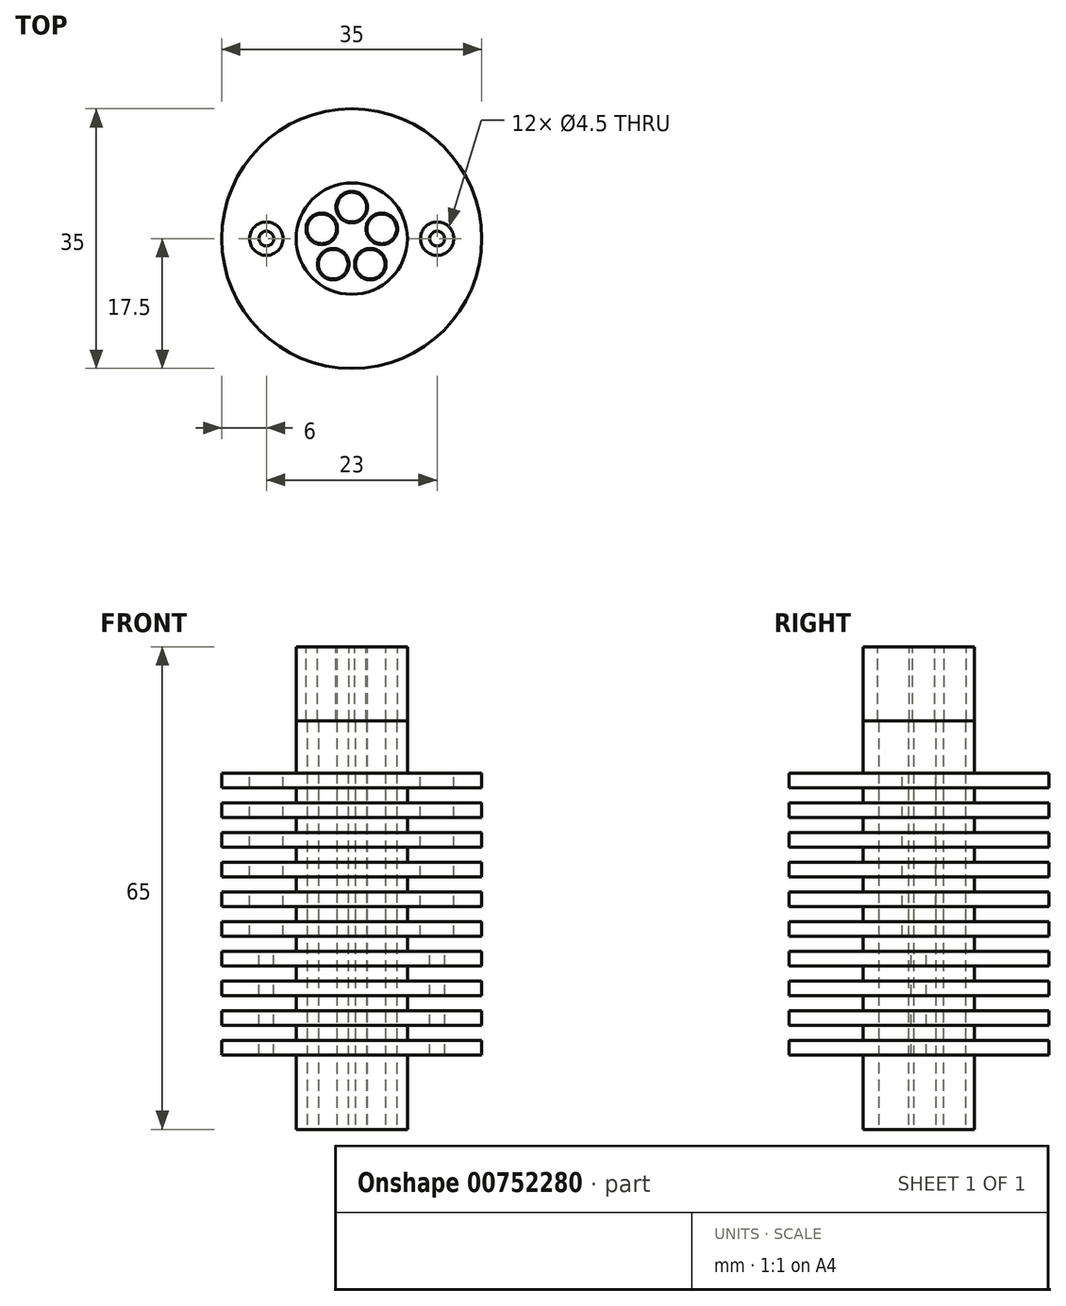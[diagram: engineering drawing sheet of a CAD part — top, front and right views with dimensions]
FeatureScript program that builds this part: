
annotation { "Feature Type Name" : "Feature", "Feature Type Description" : "" }
export const myFeature = defineFeature(function(context is Context, id is Id, definition is map)
    precondition{}
    {
        {
            var Q0;
            Q0=qCreatedBy(makeId("Top.planeOp"),FACE);
            var sketch = newSketch(context, id + "F0", { "sketchPlane" : qUnion([Q0])});
            skCircle(sketch, "E0", {"center": v(0, 0) * mm, "radius": 7.5 * mm});
            skLineSegment(sketch, "E1", {"start": v(0, 0) * mm, "end": v(0, 4.25) * mm});
            skCircle(sketch, "E2", {"center": v(0, 4.25) * mm, "radius": 2 * mm});
            skCircle(sketch, "E3.1.0", {"center": v(-4.04, 1.31) * mm, "radius": 2 * mm});
            skCircle(sketch, "E3.2.0", {"center": v(-2.5, -3.44) * mm, "radius": 2 * mm});
            skCircle(sketch, "E3.3.0", {"center": v(2.5, -3.44) * mm, "radius": 2 * mm});
            skCircle(sketch, "E3.4.0", {"center": v(4.04, 1.31) * mm, "radius": 2 * mm});
            skSolve(sketch);
        }
        {
            var Q0;
            Q0=makeQuery(id+"F0.imprint","IMPRINT",FACE,{"disambiguationData":[TD([[makeQuery(id+"F0.imprint","IMPRINT",EDGE,{"derivedFrom":sQuery(id+"F0.wireOp",EDGE,"E0")}),1.0]])]});
            extrude(context, id + "F1", {"entities" : qUnion([Q0]), "depth" : 50 * mm, "offsetDistance" : 25 * mm});
        }
        {
            var Q0;
            Q0=qCreatedBy(makeId("Front.planeOp"),FACE);
            var sketch = newSketch(context, id + "F2", { "sketchPlane" : qUnion([Q0])});
            skLineSegment(sketch, "E4.bottom", {"start": v(7.5, 5) * mm, "end": v(17.5, 5) * mm});
            skLineSegment(sketch, "E4.top", {"start": v(7.5, 7) * mm, "end": v(17.5, 7) * mm});
            skLineSegment(sketch, "E4.left", {"start": v(7.5, 5) * mm, "end": v(7.5, 7) * mm});
            skLineSegment(sketch, "E4.right", {"start": v(17.5, 5) * mm, "end": v(17.5, 7) * mm});
            skLineSegment(sketch, "E5.1.0.0", {"start": v(7.5, 11) * mm, "end": v(17.5, 11) * mm});
            skLineSegment(sketch, "E5.1.0.1", {"start": v(17.5, 9) * mm, "end": v(17.5, 11) * mm});
            skLineSegment(sketch, "E5.1.0.2", {"start": v(7.5, 9) * mm, "end": v(17.5, 9) * mm});
            skLineSegment(sketch, "E5.1.0.3", {"start": v(7.5, 9) * mm, "end": v(7.5, 11) * mm});
            skLineSegment(sketch, "E5.2.0.0", {"start": v(7.5, 15) * mm, "end": v(17.5, 15) * mm});
            skLineSegment(sketch, "E5.2.0.1", {"start": v(17.5, 13) * mm, "end": v(17.5, 15) * mm});
            skLineSegment(sketch, "E5.2.0.2", {"start": v(7.5, 13) * mm, "end": v(17.5, 13) * mm});
            skLineSegment(sketch, "E5.2.0.3", {"start": v(7.5, 13) * mm, "end": v(7.5, 15) * mm});
            skLineSegment(sketch, "E5.3.0.0", {"start": v(7.5, 19) * mm, "end": v(17.5, 19) * mm});
            skLineSegment(sketch, "E5.3.0.1", {"start": v(17.5, 17) * mm, "end": v(17.5, 19) * mm});
            skLineSegment(sketch, "E5.3.0.2", {"start": v(7.5, 17) * mm, "end": v(17.5, 17) * mm});
            skLineSegment(sketch, "E5.3.0.3", {"start": v(7.5, 17) * mm, "end": v(7.5, 19) * mm});
            skLineSegment(sketch, "E5.4.0.0", {"start": v(7.5, 23) * mm, "end": v(17.5, 23) * mm});
            skLineSegment(sketch, "E5.4.0.1", {"start": v(17.5, 21) * mm, "end": v(17.5, 23) * mm});
            skLineSegment(sketch, "E5.4.0.2", {"start": v(7.5, 21) * mm, "end": v(17.5, 21) * mm});
            skLineSegment(sketch, "E5.4.0.3", {"start": v(7.5, 21) * mm, "end": v(7.5, 23) * mm});
            skLineSegment(sketch, "E5.5.0.0", {"start": v(7.5, 27) * mm, "end": v(17.5, 27) * mm});
            skLineSegment(sketch, "E5.5.0.1", {"start": v(17.5, 25) * mm, "end": v(17.5, 27) * mm});
            skLineSegment(sketch, "E5.5.0.2", {"start": v(7.5, 25) * mm, "end": v(17.5, 25) * mm});
            skLineSegment(sketch, "E5.5.0.3", {"start": v(7.5, 25) * mm, "end": v(7.5, 27) * mm});
            skLineSegment(sketch, "E5.6.0.0", {"start": v(7.5, 31) * mm, "end": v(17.5, 31) * mm});
            skLineSegment(sketch, "E5.6.0.1", {"start": v(17.5, 29) * mm, "end": v(17.5, 31) * mm});
            skLineSegment(sketch, "E5.6.0.2", {"start": v(7.5, 29) * mm, "end": v(17.5, 29) * mm});
            skLineSegment(sketch, "E5.6.0.3", {"start": v(7.5, 29) * mm, "end": v(7.5, 31) * mm});
            skLineSegment(sketch, "E5.7.0.0", {"start": v(7.5, 35) * mm, "end": v(17.5, 35) * mm});
            skLineSegment(sketch, "E5.7.0.1", {"start": v(17.5, 33) * mm, "end": v(17.5, 35) * mm});
            skLineSegment(sketch, "E5.7.0.2", {"start": v(7.5, 33) * mm, "end": v(17.5, 33) * mm});
            skLineSegment(sketch, "E5.7.0.3", {"start": v(7.5, 33) * mm, "end": v(7.5, 35) * mm});
            skLineSegment(sketch, "E5.8.0.0", {"start": v(7.5, 39) * mm, "end": v(17.5, 39) * mm});
            skLineSegment(sketch, "E5.8.0.1", {"start": v(17.5, 37) * mm, "end": v(17.5, 39) * mm});
            skLineSegment(sketch, "E5.8.0.2", {"start": v(7.5, 37) * mm, "end": v(17.5, 37) * mm});
            skLineSegment(sketch, "E5.8.0.3", {"start": v(7.5, 37) * mm, "end": v(7.5, 39) * mm});
            skLineSegment(sketch, "E5.9.0.0", {"start": v(7.5, 43) * mm, "end": v(17.5, 43) * mm});
            skLineSegment(sketch, "E5.9.0.1", {"start": v(17.5, 41) * mm, "end": v(17.5, 43) * mm});
            skLineSegment(sketch, "E5.9.0.2", {"start": v(7.5, 41) * mm, "end": v(17.5, 41) * mm});
            skLineSegment(sketch, "E5.9.0.3", {"start": v(7.5, 41) * mm, "end": v(7.5, 43) * mm});
            skLineSegment(sketch, "E5.direction1", {"start": v(7.5, 5) * mm, "end": v(7.5, 9) * mm, "construction": true});
            skLineSegment(sketch, "E6", {"start": v(0, 0) * mm, "end": v(0, 60.8) * mm});
            skLineSegment(sketch, "E7.0.10.0", {"start": v(7.5, 47) * mm, "end": v(17.5, 47) * mm});
            skLineSegment(sketch, "E7.3.10.0", {"start": v(17.5, 45) * mm, "end": v(17.5, 47) * mm});
            skLineSegment(sketch, "E7.6.10.0", {"start": v(7.5, 45) * mm, "end": v(17.5, 45) * mm});
            skLineSegment(sketch, "E7.9.10.0", {"start": v(7.5, 45) * mm, "end": v(7.5, 47) * mm});
            skSolve(sketch);
        }
        {
            var Q0;
            Q0=makeQuery(id+"F2.imprint","IMPRINT",FACE,{"disambiguationData":[TD([[makeQuery(id+"F2.imprint","IMPRINT",EDGE,{"derivedFrom":sQuery(id+"F2.wireOp",EDGE,"E4.bottom")}),1.0]])]});
            var Q1;
            Q1=makeQuery(id+"F2.imprint","IMPRINT",FACE,{"disambiguationData":[TD([[makeQuery(id+"F2.imprint","IMPRINT",EDGE,{"derivedFrom":sQuery(id+"F2.wireOp",EDGE,"E5.1.0.0")}),-1.0]])]});
            var Q2;
            Q2=makeQuery(id+"F2.imprint","IMPRINT",FACE,{"disambiguationData":[TD([[makeQuery(id+"F2.imprint","IMPRINT",EDGE,{"derivedFrom":sQuery(id+"F2.wireOp",EDGE,"E5.2.0.0")}),-1.0]])]});
            var Q3;
            Q3=makeQuery(id+"F2.imprint","IMPRINT",FACE,{"disambiguationData":[TD([[makeQuery(id+"F2.imprint","IMPRINT",EDGE,{"derivedFrom":sQuery(id+"F2.wireOp",EDGE,"E5.3.0.0")}),-1.0]])]});
            var Q4;
            Q4=makeQuery(id+"F2.imprint","IMPRINT",FACE,{"disambiguationData":[TD([[makeQuery(id+"F2.imprint","IMPRINT",EDGE,{"derivedFrom":sQuery(id+"F2.wireOp",EDGE,"E5.4.0.0")}),-1.0]])]});
            var Q5;
            Q5=makeQuery(id+"F2.imprint","IMPRINT",FACE,{"disambiguationData":[TD([[makeQuery(id+"F2.imprint","IMPRINT",EDGE,{"derivedFrom":sQuery(id+"F2.wireOp",EDGE,"E5.5.0.0")}),-1.0]])]});
            var Q6;
            Q6=makeQuery(id+"F2.imprint","IMPRINT",FACE,{"disambiguationData":[TD([[makeQuery(id+"F2.imprint","IMPRINT",EDGE,{"derivedFrom":sQuery(id+"F2.wireOp",EDGE,"E5.6.0.0")}),-1.0]])]});
            var Q7;
            Q7=makeQuery(id+"F2.imprint","IMPRINT",FACE,{"disambiguationData":[TD([[makeQuery(id+"F2.imprint","IMPRINT",EDGE,{"derivedFrom":sQuery(id+"F2.wireOp",EDGE,"E5.7.0.0")}),-1.0]])]});
            var Q8;
            Q8=makeQuery(id+"F2.imprint","IMPRINT",FACE,{"disambiguationData":[TD([[makeQuery(id+"F2.imprint","IMPRINT",EDGE,{"derivedFrom":sQuery(id+"F2.wireOp",EDGE,"E5.8.0.0")}),-1.0]])]});
            var Q9;
            Q9=makeQuery(id+"F2.imprint","IMPRINT",FACE,{"disambiguationData":[TD([[makeQuery(id+"F2.imprint","IMPRINT",EDGE,{"derivedFrom":sQuery(id+"F2.wireOp",EDGE,"E5.9.0.0")}),-1.0]])]});
            var Q10;
            Q10=makeQuery(id+"F2.imprint","IMPRINT",FACE,{"disambiguationData":[TD([[makeQuery(id+"F2.imprint","IMPRINT",EDGE,{"derivedFrom":sQuery(id+"F2.wireOp",EDGE,"E5.10.0.0")}),-1.0]])]});
            var Q11;
            Q11=makeQuery(id+"F2.imprint","IMPRINT",FACE,{"disambiguationData":[TD([[makeQuery(id+"F2.imprint","IMPRINT",EDGE,{"derivedFrom":sQuery(id+"F2.wireOp",EDGE,"E5.11.0.0")}),-1.0]])]});
            var Q12;
            Q12=makeQuery(id+"F2.imprint","IMPRINT",FACE,{"disambiguationData":[TD([[makeQuery(id+"F2.imprint","IMPRINT",EDGE,{"derivedFrom":sQuery(id+"F2.wireOp",EDGE,"E5.23.0.0")}),-1.0]])]});
            var Q13;
            Q13=makeQuery(id+"F2.imprint","IMPRINT",FACE,{"disambiguationData":[TD([[makeQuery(id+"F2.imprint","IMPRINT",EDGE,{"derivedFrom":sQuery(id+"F2.wireOp",EDGE,"E5.24.0.0")}),-1.0]])]});
            var Q14;
            Q14=makeQuery(id+"F2.imprint","IMPRINT",FACE,{"disambiguationData":[TD([[makeQuery(id+"F2.imprint","IMPRINT",EDGE,{"derivedFrom":sQuery(id+"F2.wireOp",EDGE,"E5.25.0.0")}),-1.0]])]});
            var Q15;
            Q15=makeQuery(id+"F2.imprint","IMPRINT",FACE,{"disambiguationData":[TD([[makeQuery(id+"F2.imprint","IMPRINT",EDGE,{"derivedFrom":sQuery(id+"F2.wireOp",EDGE,"E5.26.0.0")}),-1.0]])]});
            var Q16;
            Q16=makeQuery(id+"F2.imprint","IMPRINT",FACE,{"disambiguationData":[TD([[makeQuery(id+"F2.imprint","IMPRINT",EDGE,{"derivedFrom":sQuery(id+"F2.wireOp",EDGE,"E5.27.0.0")}),-1.0]])]});
            var Q17;
            Q17=makeQuery(id+"F2.imprint","IMPRINT",FACE,{"disambiguationData":[TD([[makeQuery(id+"F2.imprint","IMPRINT",EDGE,{"derivedFrom":sQuery(id+"F2.wireOp",EDGE,"E5.28.0.0")}),-1.0]])]});
            var Q18;
            Q18=makeQuery(id+"F2.imprint","IMPRINT",FACE,{"disambiguationData":[TD([[makeQuery(id+"F2.imprint","IMPRINT",EDGE,{"derivedFrom":sQuery(id+"F2.wireOp",EDGE,"E5.16.0.0")}),-1.0]])]});
            var Q19;
            Q19=makeQuery(id+"F2.imprint","IMPRINT",FACE,{"disambiguationData":[TD([[makeQuery(id+"F2.imprint","IMPRINT",EDGE,{"derivedFrom":sQuery(id+"F2.wireOp",EDGE,"E5.17.0.0")}),-1.0]])]});
            var Q20;
            Q20=makeQuery(id+"F2.imprint","IMPRINT",FACE,{"disambiguationData":[TD([[makeQuery(id+"F2.imprint","IMPRINT",EDGE,{"derivedFrom":sQuery(id+"F2.wireOp",EDGE,"E5.18.0.0")}),-1.0]])]});
            var Q21;
            Q21=makeQuery(id+"F2.imprint","IMPRINT",FACE,{"disambiguationData":[TD([[makeQuery(id+"F2.imprint","IMPRINT",EDGE,{"derivedFrom":sQuery(id+"F2.wireOp",EDGE,"E5.13.0.0")}),-1.0]])]});
            var Q22;
            Q22=makeQuery(id+"F2.imprint","IMPRINT",FACE,{"disambiguationData":[TD([[makeQuery(id+"F2.imprint","IMPRINT",EDGE,{"derivedFrom":sQuery(id+"F2.wireOp",EDGE,"E5.14.0.0")}),-1.0]])]});
            var Q23;
            Q23=makeQuery(id+"F2.imprint","IMPRINT",FACE,{"disambiguationData":[TD([[makeQuery(id+"F2.imprint","IMPRINT",EDGE,{"derivedFrom":sQuery(id+"F2.wireOp",EDGE,"E5.12.0.0")}),-1.0]])]});
            var Q24;
            Q24=makeQuery(id+"F2.imprint","IMPRINT",FACE,{"disambiguationData":[TD([[makeQuery(id+"F2.imprint","IMPRINT",EDGE,{"derivedFrom":sQuery(id+"F2.wireOp",EDGE,"E5.19.0.0")}),-1.0]])]});
            var Q25;
            Q25=makeQuery(id+"F2.imprint","IMPRINT",FACE,{"disambiguationData":[TD([[makeQuery(id+"F2.imprint","IMPRINT",EDGE,{"derivedFrom":sQuery(id+"F2.wireOp",EDGE,"E5.20.0.0")}),-1.0]])]});
            var Q26;
            Q26=makeQuery(id+"F2.imprint","IMPRINT",FACE,{"disambiguationData":[TD([[makeQuery(id+"F2.imprint","IMPRINT",EDGE,{"derivedFrom":sQuery(id+"F2.wireOp",EDGE,"E5.21.0.0")}),-1.0]])]});
            var Q27;
            Q27=makeQuery(id+"F2.imprint","IMPRINT",FACE,{"disambiguationData":[TD([[makeQuery(id+"F2.imprint","IMPRINT",EDGE,{"derivedFrom":sQuery(id+"F2.wireOp",EDGE,"E5.22.0.0")}),-1.0]])]});
            var Q28;
            Q28=makeQuery(id+"F2.imprint","IMPRINT",FACE,{"disambiguationData":[TD([[makeQuery(id+"F2.imprint","IMPRINT",EDGE,{"derivedFrom":sQuery(id+"F2.wireOp",EDGE,"E5.29.0.0")}),-1.0]])]});
            var Q29;
            Q29=makeQuery(id+"F2.imprint","IMPRINT",FACE,{"disambiguationData":[TD([[makeQuery(id+"F2.imprint","IMPRINT",EDGE,{"derivedFrom":sQuery(id+"F2.wireOp",EDGE,"E5.15.0.0")}),-1.0]])]});
            var Q30;
            Q30=makeQuery(id+"F2.imprint","IMPRINT",FACE,{"disambiguationData":[TD([[makeQuery(id+"F2.imprint","IMPRINT",EDGE,{"derivedFrom":sQuery(id+"F2.wireOp",EDGE,"bcf629a2-7b1e-4396-892b-a52c0da3cd06.0.21.0")}),-1.0]])]});
            var Q31;
            Q31=makeQuery(id+"F2.imprint","IMPRINT",FACE,{"disambiguationData":[TD([[makeQuery(id+"F2.imprint","IMPRINT",EDGE,{"derivedFrom":sQuery(id+"F2.wireOp",EDGE,"bcf629a2-7b1e-4396-892b-a52c0da3cd06.0.20.0")}),-1.0]])]});
            var Q32;
            Q32=makeQuery(id+"F2.imprint","IMPRINT",FACE,{"disambiguationData":[TD([[makeQuery(id+"F2.imprint","IMPRINT",EDGE,{"derivedFrom":sQuery(id+"F2.wireOp",EDGE,"bcf629a2-7b1e-4396-892b-a52c0da3cd06.0.22.0")}),-1.0]])]});
            var Q33;
            Q33=sQuery(id+"F2.wireOp",EDGE,"E6");
            revolve(context, id + "F3", {"operationType" : NewBodyOperationType.ADD, "surfaceOperationType" : NewSurfaceOperationType.NEW, "entities" : qUnion([Q0, Q1, Q2, Q3, Q4, Q5, Q6, Q7, Q8, Q9, Q10, Q11, Q12, Q13, Q14, Q15, Q16, Q17, Q18, Q19, Q20, Q21, Q22, Q23, Q24, Q25, Q26, Q27, Q28, Q29, Q30, Q31, Q32]), "axis" : qUnion([Q33]), "revolveType" : RevolveType.FULL});
        }
        {
            var Q0;
            Q0=makeQuery(id+"F1.opExtrude","CAP_FACE",FACE,{"disambiguationData":[OSD([sQuery(id+"F0.wireOp",EDGE,"E0"),sQuery(id+"F0.wireOp",EDGE,"E2"),sQuery(id+"F0.wireOp",EDGE,"dMZ9IvUV-o9mW-zyb8-s1qC-M41qP8uoqj3L"),sQuery(id+"F0.wireOp",EDGE,"vm20BbzZ-NuKy-vaz8-9cYI-lsmH05uH8iyZ"),sQuery(id+"F0.wireOp",EDGE,"ybyqxBIH-QSEQ-sCN9-Jukn-hR0LF9qkr8OU"),sQuery(id+"F0.wireOp",EDGE,"9PJC6J2Q-n4DZ-XNnT-Oemt-Ry2Y1Me2nibd")])],"isStart":true});
            extrude(context, id + "F4", {"entities" : qUnion([Q0]), "operationType" : NewBodyOperationType.ADD, "depth" : 5 * mm, "offsetDistance" : 25 * mm});
        }
        {
            var Q0;
            Q0=makeQuery(id+"F3.opRevolve","SWEPT_FACE",FACE,{"disambiguationData":[OSD([sQuery(id+"F2.wireOp",EDGE,"E5.9.0.0")])]});
            var sketch = newSketch(context, id + "F5", { "sketchPlane" : qUnion([Q0])});
            skPoint(sketch, "E8", {"position": v(11.5, 0) * mm});
            skPoint(sketch, "E9", {"position": v(-11.5, 0) * mm});
            skCircle(sketch, "E10.0", {"center": v(0, 0) * mm, "radius": 7.5 * mm});
            skSolve(sketch);
        }
        {
            var Q0;
            Q0=sQuery(id+"F5.wireOp",VERTEX,"E9");
            var Q1;
            Q1=sQuery(id+"F5.wireOp",VERTEX,"E8");
            var Q2;
            Q2=makeQuery(id+"F1.opExtrude","SWEPT_BODY",BODY,{"disambiguationData":[OSD([sQuery(id+"F0.wireOp",EDGE,"E0"),sQuery(id+"F0.wireOp",EDGE,"E2"),sQuery(id+"F0.wireOp",EDGE,"E3.1.0"),sQuery(id+"F0.wireOp",EDGE,"E3.2.0"),sQuery(id+"F0.wireOp",EDGE,"E3.3.0"),sQuery(id+"F0.wireOp",EDGE,"E3.4.0")])]});
            hole(context, id + "F6", {"style" : HoleStyle.SIMPLE, "endStyle" : HoleEndStyle.THROUGH, "holeDiameter" : 2 * mm, "majorDiameter" : 5 * mm, "isTappedThrough" : true, "tappedDepth" : 12 * mm, "tapClearance" : 3, "locations" : qUnion([Q0, Q1]), "scope" : qUnion([Q2])});
        }
        {
            var Q0;
            Q0=sQuery(id+"F5.wireOp",VERTEX,"E9");
            var Q1;
            Q1=sQuery(id+"F5.wireOp",VERTEX,"E8");
            var Q2;
            Q2=makeQuery(id+"F1.opExtrude","SWEPT_BODY",BODY,{"disambiguationData":[OSD([sQuery(id+"F0.wireOp",EDGE,"E0"),sQuery(id+"F0.wireOp",EDGE,"E2"),sQuery(id+"F0.wireOp",EDGE,"E3.1.0"),sQuery(id+"F0.wireOp",EDGE,"E3.2.0"),sQuery(id+"F0.wireOp",EDGE,"E3.3.0"),sQuery(id+"F0.wireOp",EDGE,"E3.4.0")])]});
            hole(context, id + "F7", {"style" : HoleStyle.SIMPLE, "endStyle" : HoleEndStyle.BLIND, "holeDiameter" : 4.5 * mm, "majorDiameter" : 5 * mm, "holeDepth" : 22 * mm, "isTappedThrough" : true, "tappedDepth" : 12 * mm, "tapClearance" : 3, "locations" : qUnion([Q0, Q1]), "scope" : qUnion([Q2])});
        }
        {
            var Q0;
            Q0=makeQuery(id+"F1.opExtrude","CAP_FACE",FACE,{"disambiguationData":[OSD([sQuery(id+"F0.wireOp",EDGE,"E0"),sQuery(id+"F0.wireOp",EDGE,"E2"),sQuery(id+"F0.wireOp",EDGE,"E3.1.0"),sQuery(id+"F0.wireOp",EDGE,"E3.2.0"),sQuery(id+"F0.wireOp",EDGE,"E3.3.0"),sQuery(id+"F0.wireOp",EDGE,"E3.4.0")])],"isStart":false});
            extrude(context, id + "F8", {"entities" : qUnion([Q0]), "depth" : 10 * mm, "offsetDistance" : 25 * mm});
        }
        {
            var Q0;
            Q0=makeQuery(id+"F8.opExtrude","CAP_FACE",FACE,{"disambiguationData":[OSD([sQuery(id+"F0.wireOp",EDGE,"E0"),sQuery(id+"F0.wireOp",EDGE,"E2"),sQuery(id+"F0.wireOp",EDGE,"E3.1.0"),sQuery(id+"F0.wireOp",EDGE,"E3.2.0"),sQuery(id+"F0.wireOp",EDGE,"E3.3.0"),sQuery(id+"F0.wireOp",EDGE,"E3.4.0")])],"isStart":false});
            var sketch = newSketch(context, id + "F9", { "sketchPlane" : qUnion([Q0])});
            skCircle(sketch, "E11.0", {"center": v(0, 4.25) * mm, "radius": 2 * mm});
            skCircle(sketch, "E12.0", {"center": v(4.04, 1.31) * mm, "radius": 2 * mm});
            skCircle(sketch, "E12.1", {"center": v(-2.5, -3.44) * mm, "radius": 2 * mm});
            skCircle(sketch, "E12.2", {"center": v(2.5, -3.44) * mm, "radius": 2 * mm});
            skCircle(sketch, "E12.3", {"center": v(-4.04, 1.31) * mm, "radius": 2 * mm});
            skSolve(sketch);
        }
        {
            var Q0;
            Q0=sQuery(id+"F9.wireOp",VERTEX,"E11.0.center");
            var Q1;
            Q1=sQuery(id+"F9.wireOp",VERTEX,"E12.0.center");
            var Q2;
            Q2=sQuery(id+"F9.wireOp",VERTEX,"E12.2.center");
            var Q3;
            Q3=sQuery(id+"F9.wireOp",VERTEX,"E12.1.center");
            var Q4;
            Q4=sQuery(id+"F9.wireOp",VERTEX,"E12.3.center");
            var Q5;
            Q5=makeQuery(id+"F8.opExtrude","SWEPT_BODY",BODY,{"disambiguationData":[OSD([sQuery(id+"F0.wireOp",EDGE,"E0"),sQuery(id+"F0.wireOp",EDGE,"E2"),sQuery(id+"F0.wireOp",EDGE,"E3.1.0"),sQuery(id+"F0.wireOp",EDGE,"E3.2.0"),sQuery(id+"F0.wireOp",EDGE,"E3.3.0"),sQuery(id+"F0.wireOp",EDGE,"E3.4.0")])]});
            hole(context, id + "F10", {"style" : HoleStyle.SIMPLE, "endStyle" : HoleEndStyle.THROUGH, "holeDiameter" : 4.25 * mm, "majorDiameter" : 5 * mm, "isTappedThrough" : true, "tappedDepth" : 12 * mm, "tapClearance" : 3, "locations" : qUnion([Q0, Q1, Q2, Q3, Q4]), "scope" : qUnion([Q5])});
        }
    });
